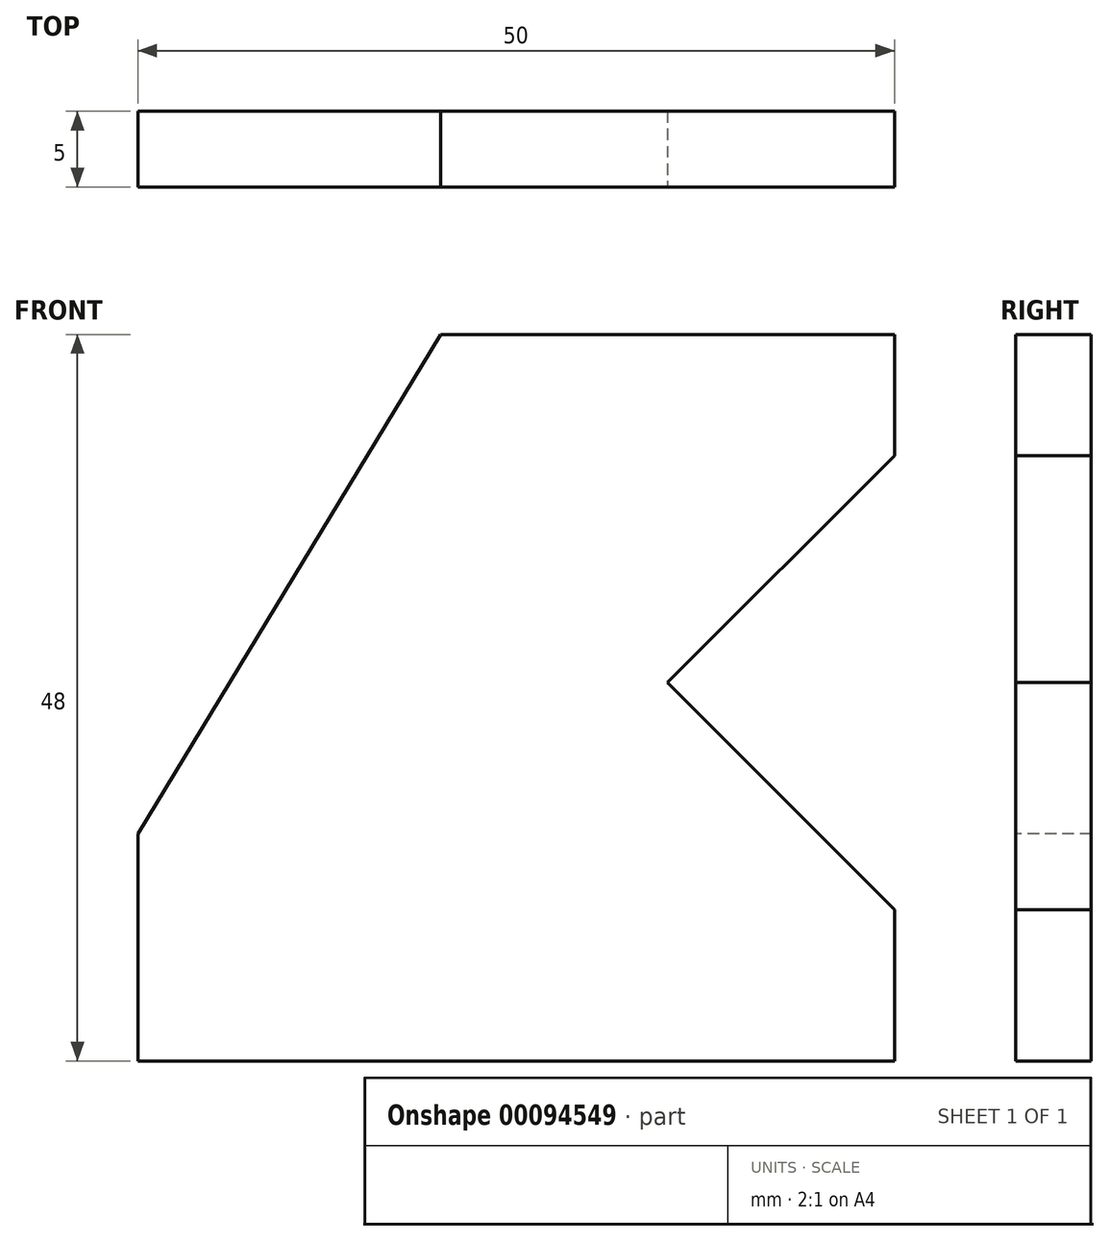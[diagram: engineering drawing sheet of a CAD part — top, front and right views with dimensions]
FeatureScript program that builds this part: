
annotation { "Feature Type Name" : "Feature", "Feature Type Description" : "" }
export const myFeature = defineFeature(function(context is Context, id is Id, definition is map)
    precondition{}
    {
        {
            var Q0;
            Q0=qCreatedBy(makeId("Front.planeOp"),FACE);
            var sketch = newSketch(context, id + "F0", { "sketchPlane" : qUnion([Q0])});
            skLineSegment(sketch, "E0.bottom", {"start": v(0, 0) * mm, "end": v(50, 0) * mm});
            skLineSegment(sketch, "E0.top", {"start": v(20, 48) * mm, "end": v(50, 48) * mm});
            skLineSegment(sketch, "E0.left", {"start": v(0, 0) * mm, "end": v(0, 15) * mm});
            skLineSegment(sketch, "E0.right", {"start": v(50, 0) * mm, "end": v(50, 10) * mm});
            skLineSegment(sketch, "E1", {"start": v(20, 48) * mm, "end": v(0, 15) * mm});
            skLineSegment(sketch, "E2", {"start": v(50, 48) * mm, "end": v(50, 40) * mm});
            skLineSegment(sketch, "E3", {"start": v(50, 0) * mm, "end": v(35, 0) * mm});
            skLineSegment(sketch, "E4.trimOffspring", {"start": v(50, 40) * mm, "end": v(50, 48) * mm});
            skPoint(sketch, "E5.endSnap0", {"position": v(35, 48) * mm});
            skLineSegment(sketch, "E6", {"start": v(35, 25) * mm, "end": v(50, 40) * mm});
            skLineSegment(sketch, "E7", {"start": v(35, 25) * mm, "end": v(50, 10) * mm});
            skSolve(sketch);
        }
        {
            var Q0;
            Q0=makeQuery(id+"F0.imprint","IMPRINT",FACE,{"disambiguationData":[TD([[makeQuery(id+"F0.imprint","IMPRINT",EDGE,{"derivedFrom":sQuery(id+"F0.wireOp",EDGE,"E0.bottom")}),1.0]])]});
            extrude(context, id + "F1", {"entities" : qUnion([Q0]), "oppositeDirection" : true, "depth" : 5 * mm});
        }
    });
